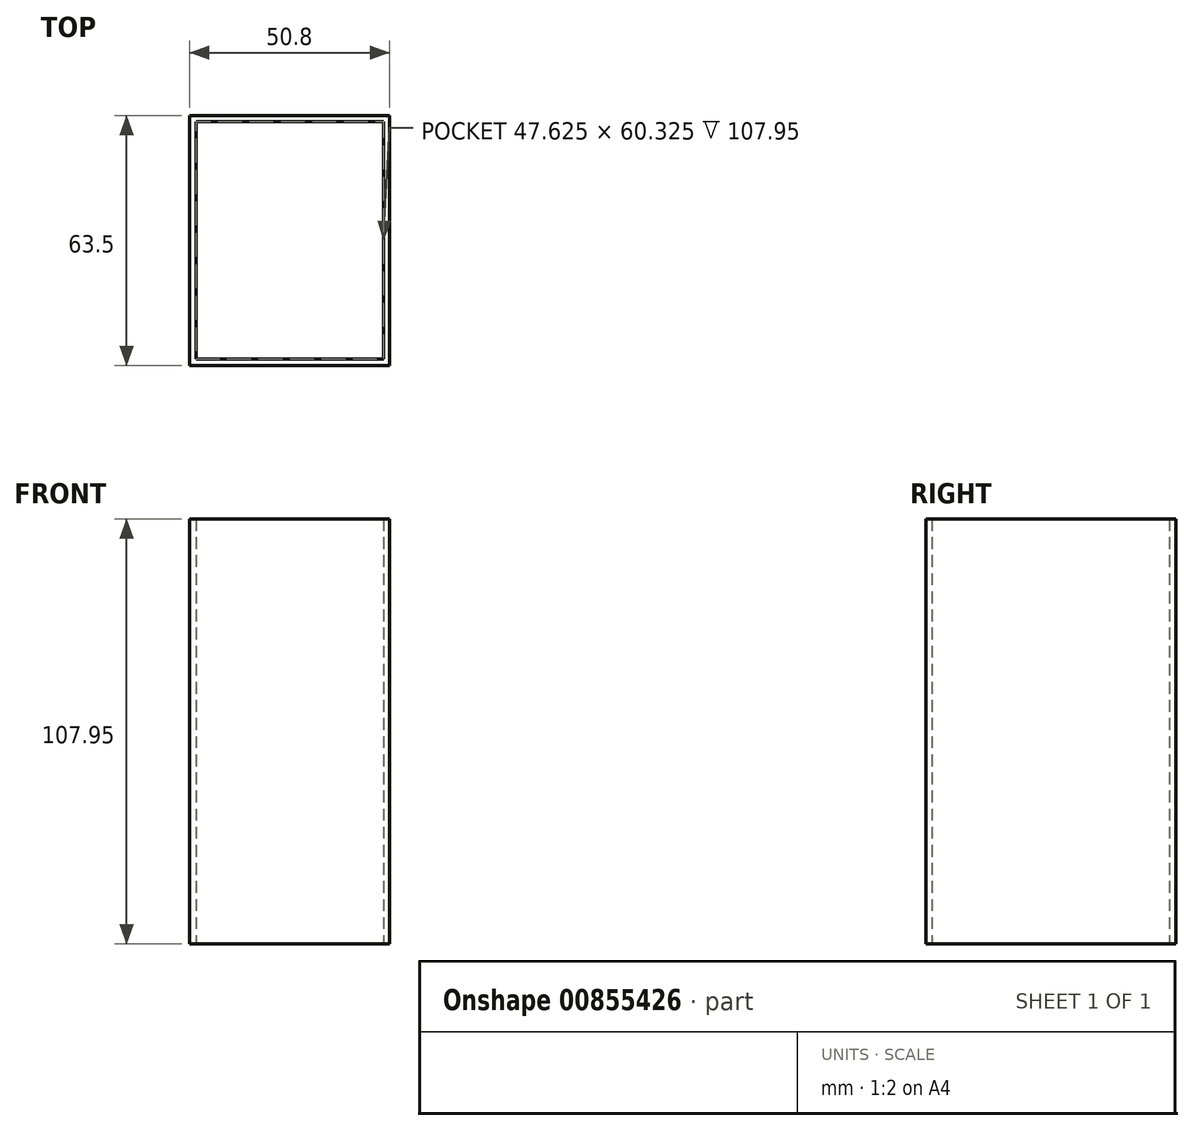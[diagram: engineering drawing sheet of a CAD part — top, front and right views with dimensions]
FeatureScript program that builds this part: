
annotation { "Feature Type Name" : "Feature", "Feature Type Description" : "" }
export const myFeature = defineFeature(function(context is Context, id is Id, definition is map)
    precondition{}
    {
        {
            var Q0;
            Q0=qCreatedBy(makeId("Top.planeOp"),FACE);
            var sketch = newSketch(context, id + "F0", { "sketchPlane" : qUnion([Q0])});
            skLineSegment(sketch, "E0.bottom", {"start": v(25.4, -31.75) * mm, "end": v(-25.4, -31.75) * mm});
            skLineSegment(sketch, "E0.top", {"start": v(25.4, 31.75) * mm, "end": v(-25.4, 31.75) * mm});
            skLineSegment(sketch, "E0.left", {"start": v(25.4, -31.75) * mm, "end": v(25.4, 31.75) * mm});
            skLineSegment(sketch, "E0.right", {"start": v(-25.4, -31.75) * mm, "end": v(-25.4, 31.75) * mm});
            skPoint(sketch, "E0.middle", {"position": v(0, 0) * mm});
            skSolve(sketch);
        }
        {
            var Q0;
            Q0 = qSketchRegion(id + "F0", true);
            extrude(context, id + "F1", {"entities" : qUnion([Q0]), "depth" : 1 / 203.2 * mm, "offsetDistance" : 25.4 * mm});
        }
        {
            var Q0;
            Q0=makeQuery(id+"F1.opExtrude","CAP_FACE",FACE,{"disambiguationData":[OSD([sQuery(id+"F0.wireOp",EDGE,"E0.bottom"),sQuery(id+"F0.wireOp",EDGE,"E0.top"),sQuery(id+"F0.wireOp",EDGE,"E0.left"),sQuery(id+"F0.wireOp",EDGE,"E0.right")])],"isStart":false});
            var sketch = newSketch(context, id + "F2", { "sketchPlane" : qUnion([Q0])});
            skLineSegment(sketch, "E1.bottom", {"start": v(23.81, -30.16) * mm, "end": v(-23.81, -30.16) * mm});
            skLineSegment(sketch, "E1.top", {"start": v(23.81, 30.16) * mm, "end": v(-23.81, 30.16) * mm});
            skLineSegment(sketch, "E1.left", {"start": v(23.81, -30.16) * mm, "end": v(23.81, 30.16) * mm});
            skLineSegment(sketch, "E1.right", {"start": v(-23.81, -30.16) * mm, "end": v(-23.81, 30.16) * mm});
            skPoint(sketch, "E1.middle", {"position": v(0, 0) * mm});
            skLineSegment(sketch, "E2.bottom", {"start": v(25.4, -31.75) * mm, "end": v(-25.4, -31.75) * mm});
            skLineSegment(sketch, "E2.top", {"start": v(25.4, 31.75) * mm, "end": v(-25.4, 31.75) * mm});
            skLineSegment(sketch, "E2.left", {"start": v(25.4, -31.75) * mm, "end": v(25.4, 31.75) * mm});
            skLineSegment(sketch, "E2.right", {"start": v(-25.4, -31.75) * mm, "end": v(-25.4, 31.75) * mm});
            skSolve(sketch);
        }
        {
            var Q0;
            Q0 = qSketchRegion(id + "F2", true);
            extrude(context, id + "F3", {"entities" : qUnion([Q0]), "operationType" : NewBodyOperationType.ADD, "depth" : 107.95 * mm, "offsetDistance" : 25.4 * mm});
        }
    });
